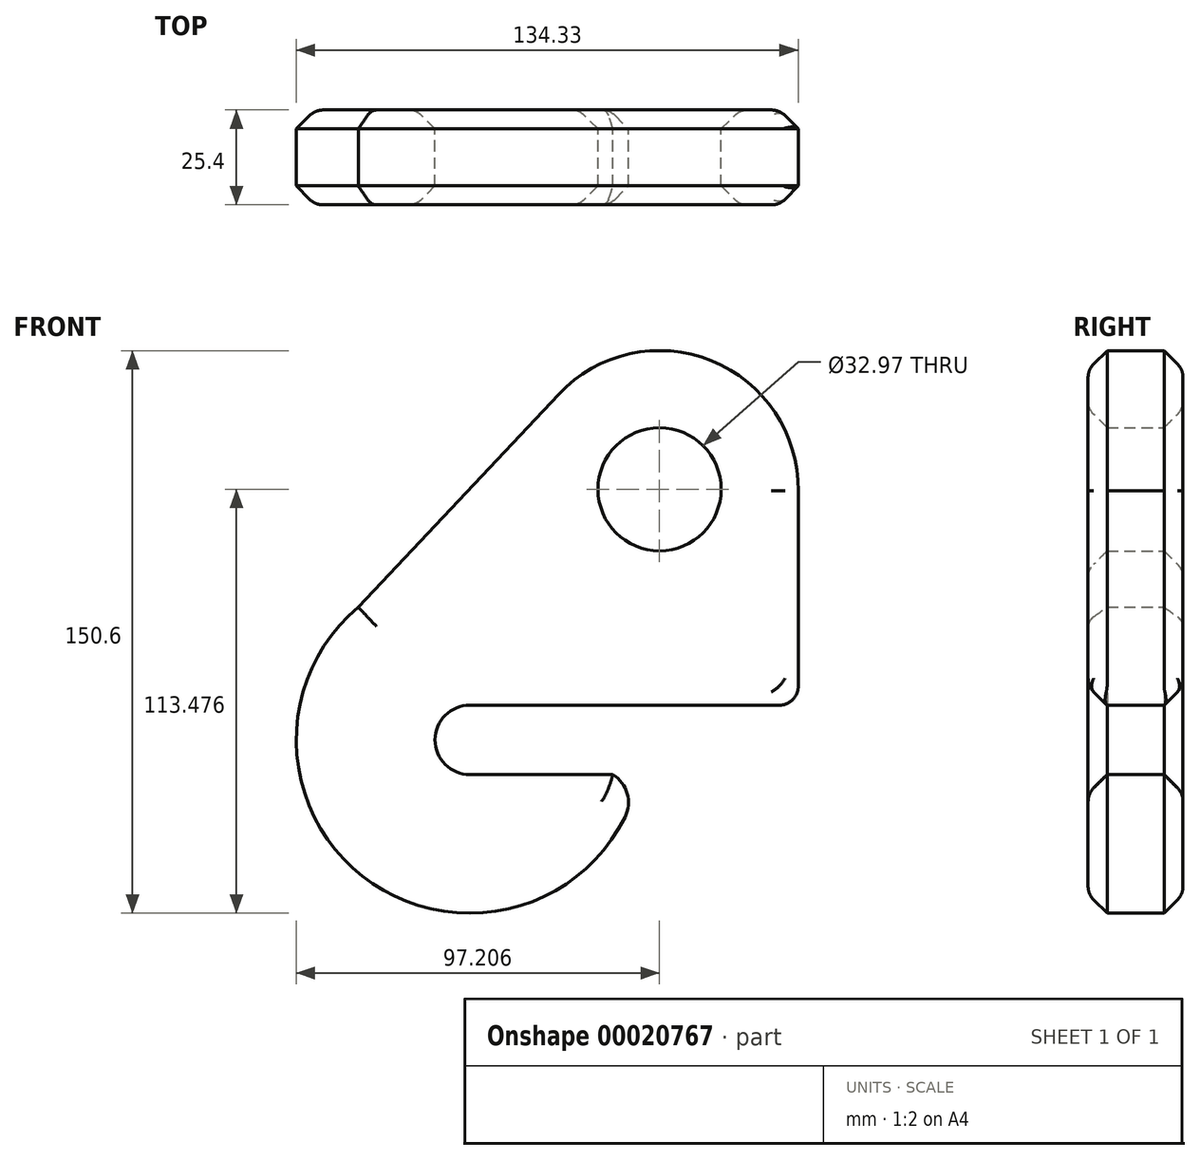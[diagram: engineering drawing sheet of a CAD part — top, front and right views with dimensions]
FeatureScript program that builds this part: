
annotation { "Feature Type Name" : "Feature", "Feature Type Description" : "" }
export const myFeature = defineFeature(function(context is Context, id is Id, definition is map)
    precondition{}
    {
        {
            var Q0;
            Q0=qCreatedBy(makeId("Front.planeOp"),FACE);
            var sketch = newSketch(context, id + "F0", { "sketchPlane" : qUnion([Q0])});
            skArc(sketch, "E0", {"start": v(60, 39.03) * mm, "mid": v(36.77, 73.89) * mm, "end": v(-4.15, 64.9) * mm});
            skArc(sketch, "E1", {"start": v(-57.75, 7.93) * mm, "mid": v(-56.63, -64.07) * mm, "end": v(13.63, -48.29) * mm});
            skArc(sketch, "E2", {"start": v(-27.91, -18.33) * mm, "mid": v(-37.2, -27.62) * mm, "end": v(-27.91, -36.9) * mm});
            skLineSegment(sketch, "E3", {"start": v(-27.91, -36.9) * mm, "end": v(10.41, -36.9) * mm});
            skArc(sketch, "E4", {"start": v(13.63, -48.29) * mm, "mid": v(14.22, -41.97) * mm, "end": v(10.41, -36.9) * mm});
            skLineSegment(sketch, "E5", {"start": v(-65.2, 0) * mm, "end": v(0, 69.3) * mm});
            skLineSegment(sketch, "E6", {"start": v(60, 39.03) * mm, "end": v(60, -18.33) * mm});
            skLineSegment(sketch, "E7", {"start": v(-27.91, -18.33) * mm, "end": v(60, -18.33) * mm});
            skCircle(sketch, "E8", {"center": v(22.89, 39.46) * mm, "radius": 16.49 * mm});
            skSolve(sketch);
        }
        {
            var Q0;
            Q0 = qSketchRegion(id + "F0", true);
            extrude(context, id + "F1", {"entities" : qUnion([Q0]), "depth" : 25.4 * mm});
        }
        {
            var Q0;
            Q0=makeQuery(id+"F1.opExtrude","CAP_FACE",FACE,{"disambiguationData":[OSD([sQuery(id+"F0.wireOp",EDGE,"E0"),sQuery(id+"F0.wireOp",EDGE,"E1"),sQuery(id+"F0.wireOp",EDGE,"E2"),sQuery(id+"F0.wireOp",EDGE,"E3"),sQuery(id+"F0.wireOp",EDGE,"E4"),sQuery(id+"F0.wireOp",EDGE,"E5"),sQuery(id+"F0.wireOp",EDGE,"E6"),sQuery(id+"F0.wireOp",EDGE,"E7"),sQuery(id+"F0.wireOp",EDGE,"E8")])],"isStart":false});
            var Q1;
            Q1=makeQuery(id+"F1.opExtrude","CAP_FACE",FACE,{"disambiguationData":[OSD([sQuery(id+"F0.wireOp",EDGE,"E0"),sQuery(id+"F0.wireOp",EDGE,"E1"),sQuery(id+"F0.wireOp",EDGE,"E2"),sQuery(id+"F0.wireOp",EDGE,"E3"),sQuery(id+"F0.wireOp",EDGE,"E4"),sQuery(id+"F0.wireOp",EDGE,"E5"),sQuery(id+"F0.wireOp",EDGE,"E6"),sQuery(id+"F0.wireOp",EDGE,"E7"),sQuery(id+"F0.wireOp",EDGE,"E8")])],"isStart":true});
            chamfer(context, id + "F2", {"entities" : qUnion([Q0, Q1]), "width" : 5.08 * mm, "tangentPropagation" : true});
        }
        {
            var Q0;
            Q0=makeQuery(id+"F1.opExtrude","SWEPT_EDGE",EDGE,{"disambiguationData":[OSD([sQuery(id+"F0.wireOp",EDGE,"E6"),sQuery(id+"F0.wireOp",EDGE,"E7")])]});
            var Q1;
            Q1=makeQuery(id+"F2.opChamfer","BLEND_EDGE",EDGE,{"blendedFrom":[makeQuery(id+"F1.opExtrude","CAP_EDGE",EDGE,{"disambiguationData":[OSD([sQuery(id+"F0.wireOp",EDGE,"E6")])],"isStart":true}),makeQuery(id+"F1.opExtrude","CAP_EDGE",EDGE,{"disambiguationData":[OSD([sQuery(id+"F0.wireOp",EDGE,"E7")])],"isStart":true})],"blendedInto":[]});
            var Q2;
            Q2=makeQuery(id+"F2.opChamfer","BLEND_EDGE",EDGE,{"blendedFrom":[makeQuery(id+"F1.opExtrude","CAP_EDGE",EDGE,{"disambiguationData":[OSD([sQuery(id+"F0.wireOp",EDGE,"E6")])],"isStart":false}),makeQuery(id+"F1.opExtrude","CAP_EDGE",EDGE,{"disambiguationData":[OSD([sQuery(id+"F0.wireOp",EDGE,"E7")])],"isStart":false})],"blendedInto":[]});
            fillet(context, id + "F3", {"entities" : qUnion([Q0, Q1, Q2]), "radius" : 5.08 * mm, "tangentPropagation" : true, "allowEdgeOverflow" : false});
        }
        {
            var Q0;
            Q0=makeQuery(id+"F1.opExtrude","CAP_FACE",FACE,{"disambiguationData":[OSD([sQuery(id+"F0.wireOp",EDGE,"E0"),sQuery(id+"F0.wireOp",EDGE,"E1"),sQuery(id+"F0.wireOp",EDGE,"E2"),sQuery(id+"F0.wireOp",EDGE,"E3"),sQuery(id+"F0.wireOp",EDGE,"E4"),sQuery(id+"F0.wireOp",EDGE,"E5"),sQuery(id+"F0.wireOp",EDGE,"E6"),sQuery(id+"F0.wireOp",EDGE,"E7"),sQuery(id+"F0.wireOp",EDGE,"E8")])],"isStart":true});
            fillet(context, id + "F4", {"entities" : qUnion([Q0]), "radius" : 5.08 * mm, "tangentPropagation" : true, "allowEdgeOverflow" : false});
        }
        {
            var Q0;
            Q0=makeQuery(id+"F1.opExtrude","CAP_FACE",FACE,{"disambiguationData":[OSD([sQuery(id+"F0.wireOp",EDGE,"E0"),sQuery(id+"F0.wireOp",EDGE,"E1"),sQuery(id+"F0.wireOp",EDGE,"E2"),sQuery(id+"F0.wireOp",EDGE,"E3"),sQuery(id+"F0.wireOp",EDGE,"E4"),sQuery(id+"F0.wireOp",EDGE,"E5"),sQuery(id+"F0.wireOp",EDGE,"E6"),sQuery(id+"F0.wireOp",EDGE,"E7"),sQuery(id+"F0.wireOp",EDGE,"E8")])],"isStart":false});
            fillet(context, id + "F5", {"entities" : qUnion([Q0]), "radius" : 5.08 * mm, "tangentPropagation" : true, "allowEdgeOverflow" : false});
        }
    });
